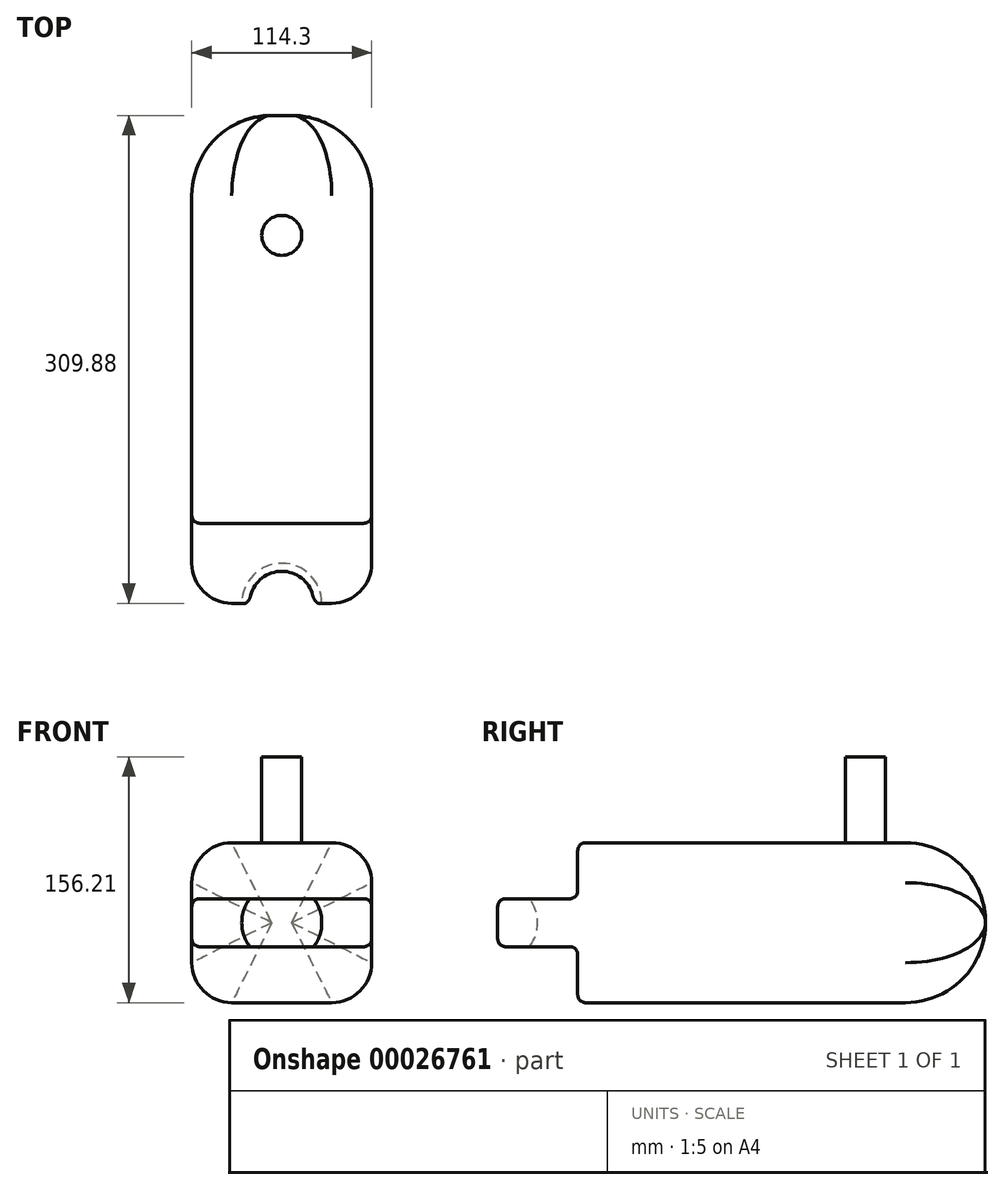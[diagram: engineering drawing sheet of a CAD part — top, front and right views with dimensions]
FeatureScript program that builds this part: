
annotation { "Feature Type Name" : "Feature", "Feature Type Description" : "" }
export const myFeature = defineFeature(function(context is Context, id is Id, definition is map)
    precondition{}
    {
        {
            var Q0;
            Q0=qCreatedBy(makeId("Front.planeOp"),FACE);
            var sketch = newSketch(context, id + "F0", { "sketchPlane" : qUnion([Q0])});
            skLineSegment(sketch, "E0.rect.bottom", {"start": v(31.75, 50.8) * mm, "end": v(-31.75, 50.8) * mm});
            skLineSegment(sketch, "E0.rect.top", {"start": v(31.75, -50.8) * mm, "end": v(-31.75, -50.8) * mm});
            skLineSegment(sketch, "E0.rect.left", {"start": v(57.15, 25.4) * mm, "end": v(57.15, -25.4) * mm});
            skLineSegment(sketch, "E0.rect.right", {"start": v(-57.15, 25.4) * mm, "end": v(-57.15, -25.4) * mm});
            skPoint(sketch, "E0.rect.middle", {"position": v(0, 0) * mm});
            skPoint(sketch, "E1.visualSharp", {"position": v(-57.15, 50.8) * mm});
            skArc(sketch, "E1.filletArc", {"start": v(-31.75, 50.8) * mm, "mid": v(-49.71, 43.36) * mm, "end": v(-57.15, 25.4) * mm});
            skPoint(sketch, "E2.visualSharp", {"position": v(57.15, 50.8) * mm});
            skArc(sketch, "E2.filletArc", {"start": v(57.15, 25.4) * mm, "mid": v(49.71, 43.36) * mm, "end": v(31.75, 50.8) * mm});
            skPoint(sketch, "E3.visualSharp", {"position": v(57.15, -50.8) * mm});
            skArc(sketch, "E3.filletArc", {"start": v(31.75, -50.8) * mm, "mid": v(49.71, -43.36) * mm, "end": v(57.15, -25.4) * mm});
            skPoint(sketch, "E4.visualSharp", {"position": v(-57.15, -50.8) * mm});
            skArc(sketch, "E4.filletArc", {"start": v(-57.15, -25.4) * mm, "mid": v(-49.71, -43.36) * mm, "end": v(-31.75, -50.8) * mm});
            skSolve(sketch);
        }
        {
            var Q0;
            Q0=makeQuery(id+"F0.imprint","IMPRINT",FACE,{"disambiguationData":[TD([[makeQuery(id+"F0.imprint","IMPRINT",EDGE,{"derivedFrom":sQuery(id+"F0.wireOp",EDGE,"E0.rect.bottom")}),1.0]])]});
            extrude(context, id + "F1", {"entities" : qUnion([Q0]), "depth" : 309.88 * mm});
        }
        {
            var Q0;
            {var subQ0=sQuery(id+"F0.wireOp",EDGE,"E0.rect.right");Q0=makeQuery(id+"FTmQkbX92Hr0Mj3_1.boolean.opBoolean","MERGE",EDGE,{"derivedFrom":[makeQuery(id+"F1.opExtrude","CAP_EDGE",EDGE,{"disambiguationData":[OSD([subQ0])],"isStart":false}),makeQuery(id+"FTmQkbX92Hr0Mj3_1.opLoft","MID_CAP_EDGE",EDGE,{"disambiguationData":[OSD([subQ0,sQuery(id+"F0.wireOp",EDGE,"E1.filletArc"),sQuery(id+"F0.wireOp",EDGE,"E4.filletArc")])],"capPos":1.0})]});}
            fillet(context, id + "F2", {"entities" : qUnion([Q0]), "radius" : 25.4 * mm, "tangentPropagation" : true, "allowEdgeOverflow" : false});
        }
        {
            var Q0;
            Q0=makeQuery(id+"F1.opExtrude","CAP_FACE",FACE,{"disambiguationData":[OSD([sQuery(id+"F0.wireOp",EDGE,"E0.rect.bottom"),sQuery(id+"F0.wireOp",EDGE,"E0.rect.top"),sQuery(id+"F0.wireOp",EDGE,"E0.rect.left"),sQuery(id+"F0.wireOp",EDGE,"E0.rect.right"),sQuery(id+"F0.wireOp",EDGE,"E1.filletArc"),sQuery(id+"F0.wireOp",EDGE,"E2.filletArc"),sQuery(id+"F0.wireOp",EDGE,"E3.filletArc"),sQuery(id+"F0.wireOp",EDGE,"E4.filletArc")])],"isStart":false});
            var sketch = newSketch(context, id + "F3", { "sketchPlane" : qUnion([Q0])});
            skCircle(sketch, "E5", {"center": v(0, 0) * mm, "radius": 25.4 * mm});
            skLineSegment(sketch, "E6", {"start": v(0, 25.4) * mm, "end": v(0, -25.4) * mm});
            skSolve(sketch);
        }
        {
            var Q0;
            {var subQ0=sQuery(id+"F3.wireOp",EDGE,"E6");Q0=makeQuery(id+"F3.imprint","IMPRINT",FACE,{"disambiguationData":[TD([[makeQuery(id+"F3.imprint","IMPRINT",EDGE,{"derivedFrom":subQ0}),1.0]])]});}
            var Q1;
            Q1=sQuery(id+"F3.wireOp",EDGE,"E6");
            revolve(context, id + "F4", {"operationType" : NewBodyOperationType.REMOVE, "entities" : qUnion([Q0]), "axis" : qUnion([Q1]), "revolveType" : RevolveType.FULL, "oppositeDirection" : true});
        }
        {
            var Q0;
            Q0=makeQuery(id+"F1.opExtrude","CAP_EDGE",EDGE,{"disambiguationData":[OSD([sQuery(id+"F0.wireOp",EDGE,"E0.rect.bottom")])],"isStart":true});
            fillet(context, id + "F5", {"entities" : qUnion([Q0]), "radius" : 50.8 * mm, "tangentPropagation" : true, "allowEdgeOverflow" : false});
        }
        {
            var Q0;
            {var subQ0=sQuery(id+"F0.wireOp",EDGE,"E0.rect.bottom");var subQ1=sQuery(id+"F0.wireOp",EDGE,"E0.rect.top");var subQ2=sQuery(id+"F0.wireOp",EDGE,"E0.rect.right");var subQ3=sQuery(id+"F0.wireOp",EDGE,"E1.filletArc");var subQ4=sQuery(id+"F0.wireOp",EDGE,"E4.filletArc");var subQ5=makeQuery(id+"F1.opExtrude","CAP_FACE",FACE,{"disambiguationData":[OSD([subQ0,subQ1,sQuery(id+"F0.wireOp",EDGE,"E0.rect.left"),subQ2,subQ3,sQuery(id+"F0.wireOp",EDGE,"E2.filletArc"),sQuery(id+"F0.wireOp",EDGE,"E3.filletArc"),subQ4])],"isStart":false});Q0=makeQuery(id+"F4.boolean.opBoolean","SPLIT",FACE,{"disambiguationData":[TD([makeQuery(id+"F2.opFillet","BLEND_FACE",FACE,{"disambiguationData":[OSD([subQ2])]})])],"derivedFrom":subQ5});}
            var sketch = newSketch(context, id + "F6", { "sketchPlane" : qUnion([Q0])});
            skLineSegment(sketch, "E7", {"start": v(0, 0) * mm, "end": v(0, 15.24) * mm});
            skLineSegment(sketch, "E8", {"start": v(0, 0) * mm, "end": v(0, -15.24) * mm});
            skLineSegment(sketch, "E9", {"start": v(1, 15.24) * mm, "end": v(-71.44, 15.24) * mm});
            skLineSegment(sketch, "E10", {"start": v(-71.44, 15.24) * mm, "end": v(-71.44, 54.5) * mm});
            skLineSegment(sketch, "E11", {"start": v(-71.44, 54.5) * mm, "end": v(64.32, 54.5) * mm});
            skLineSegment(sketch, "E12", {"start": v(64.32, 54.5) * mm, "end": v(64.32, 15.24) * mm});
            skLineSegment(sketch, "E13", {"start": v(64.32, 15.24) * mm, "end": v(0, 15.24) * mm});
            skLineSegment(sketch, "E14", {"start": v(0, -15.24) * mm, "end": v(-71.44, -15.24) * mm});
            skLineSegment(sketch, "E15", {"start": v(-71.44, -15.24) * mm, "end": v(-71.44, -54.66) * mm});
            skLineSegment(sketch, "E16", {"start": v(-71.44, -54.66) * mm, "end": v(64.32, -54.66) * mm});
            skLineSegment(sketch, "E17", {"start": v(64.32, -54.66) * mm, "end": v(64.32, -15.24) * mm});
            skLineSegment(sketch, "E18", {"start": v(64.32, -15.24) * mm, "end": v(0, -15.24) * mm});
            skSolve(sketch);
        }
        {
            var Q0;
            Q0 = qSketchRegion(id + "F6", true);
            extrude(context, id + "F7", {"entities" : qUnion([Q0]), "operationType" : NewBodyOperationType.REMOVE, "oppositeDirection" : true, "depth" : 50.8 * mm});
        }
        {
            var Q0;
            Q0=makeQuery(id+"F7.boolean.opBoolean","COPY",EDGE,{"derivedFrom":makeQuery(id+"F7.opExtrude","CAP_EDGE",EDGE,{"disambiguationData":[OSD([sQuery(id+"F6.wireOp",EDGE,"E14"),sQuery(id+"F6.wireOp",EDGE,"E18")])],"isStart":false})});
            var Q1;
            Q1=makeQuery(id+"F7.boolean.opBoolean","COPY",EDGE,{"derivedFrom":makeQuery(id+"F7.opExtrude","CAP_EDGE",EDGE,{"disambiguationData":[OSD([sQuery(id+"F6.wireOp",EDGE,"E9"),sQuery(id+"F6.wireOp",EDGE,"E13")])],"isStart":false})});
            fillet(context, id + "F8", {"entities" : qUnion([Q0, Q1]), "radius" : 5.08 * mm, "tangentPropagation" : true, "allowEdgeOverflow" : false});
        }
        {
            var Q0;
            Q0=makeQuery(id+"F1.opExtrude","SWEPT_FACE",FACE,{"disambiguationData":[OSD([sQuery(id+"F0.wireOp",EDGE,"E0.rect.bottom")])]});
            var sketch = newSketch(context, id + "F9", { "sketchPlane" : qUnion([Q0])});
            skLineSegment(sketch, "E19", {"start": v(0, -50.8) * mm, "end": v(0, -76.2) * mm});
            skCircle(sketch, "E20", {"center": v(0, -76.2) * mm, "radius": 12.7 * mm});
            skSolve(sketch);
        }
        {
            var Q0;
            Q0=makeQuery(id+"F9.imprint","IMPRINT",FACE,{"disambiguationData":[TD([[makeQuery(id+"F9.imprint","IMPRINT",EDGE,{"derivedFrom":sQuery(id+"F9.wireOp",EDGE,"E20")}),1.0]])]});
            extrude(context, id + "F10", {"entities" : qUnion([Q0]), "operationType" : NewBodyOperationType.ADD, "depth" : 54.6 * mm});
        }
        {
            var Q0;
            Q0=makeQuery(id+"F7.boolean.opBoolean","INTERSECT",EDGE,{"derivedFrom":[makeQuery(id+"F1.opExtrude","SWEPT_FACE",FACE,{"disambiguationData":[OSD([sQuery(id+"F0.wireOp",EDGE,"E0.rect.bottom")])]}),makeQuery(id+"F7.opExtrude","CAP_FACE",FACE,{"disambiguationData":[OSD([sQuery(id+"F6.wireOp",EDGE,"E9"),sQuery(id+"F6.wireOp",EDGE,"E10"),sQuery(id+"F6.wireOp",EDGE,"E11"),sQuery(id+"F6.wireOp",EDGE,"E12"),sQuery(id+"F6.wireOp",EDGE,"E13")])],"isStart":false})]});
            var Q1;
            Q1=makeQuery(id+"F7.boolean.opBoolean","INTERSECT",EDGE,{"derivedFrom":[makeQuery(id+"F1.opExtrude","SWEPT_FACE",FACE,{"disambiguationData":[OSD([sQuery(id+"F0.wireOp",EDGE,"E0.rect.top")])]}),makeQuery(id+"F7.opExtrude","CAP_FACE",FACE,{"disambiguationData":[OSD([sQuery(id+"F6.wireOp",EDGE,"E14"),sQuery(id+"F6.wireOp",EDGE,"E15"),sQuery(id+"F6.wireOp",EDGE,"E16"),sQuery(id+"F6.wireOp",EDGE,"E17"),sQuery(id+"F6.wireOp",EDGE,"E18")])],"isStart":false})]});
            fillet(context, id + "F11", {"entities" : qUnion([Q0, Q1]), "radius" : 5.08 * mm, "tangentPropagation" : true, "allowEdgeOverflow" : false});
        }
    });
